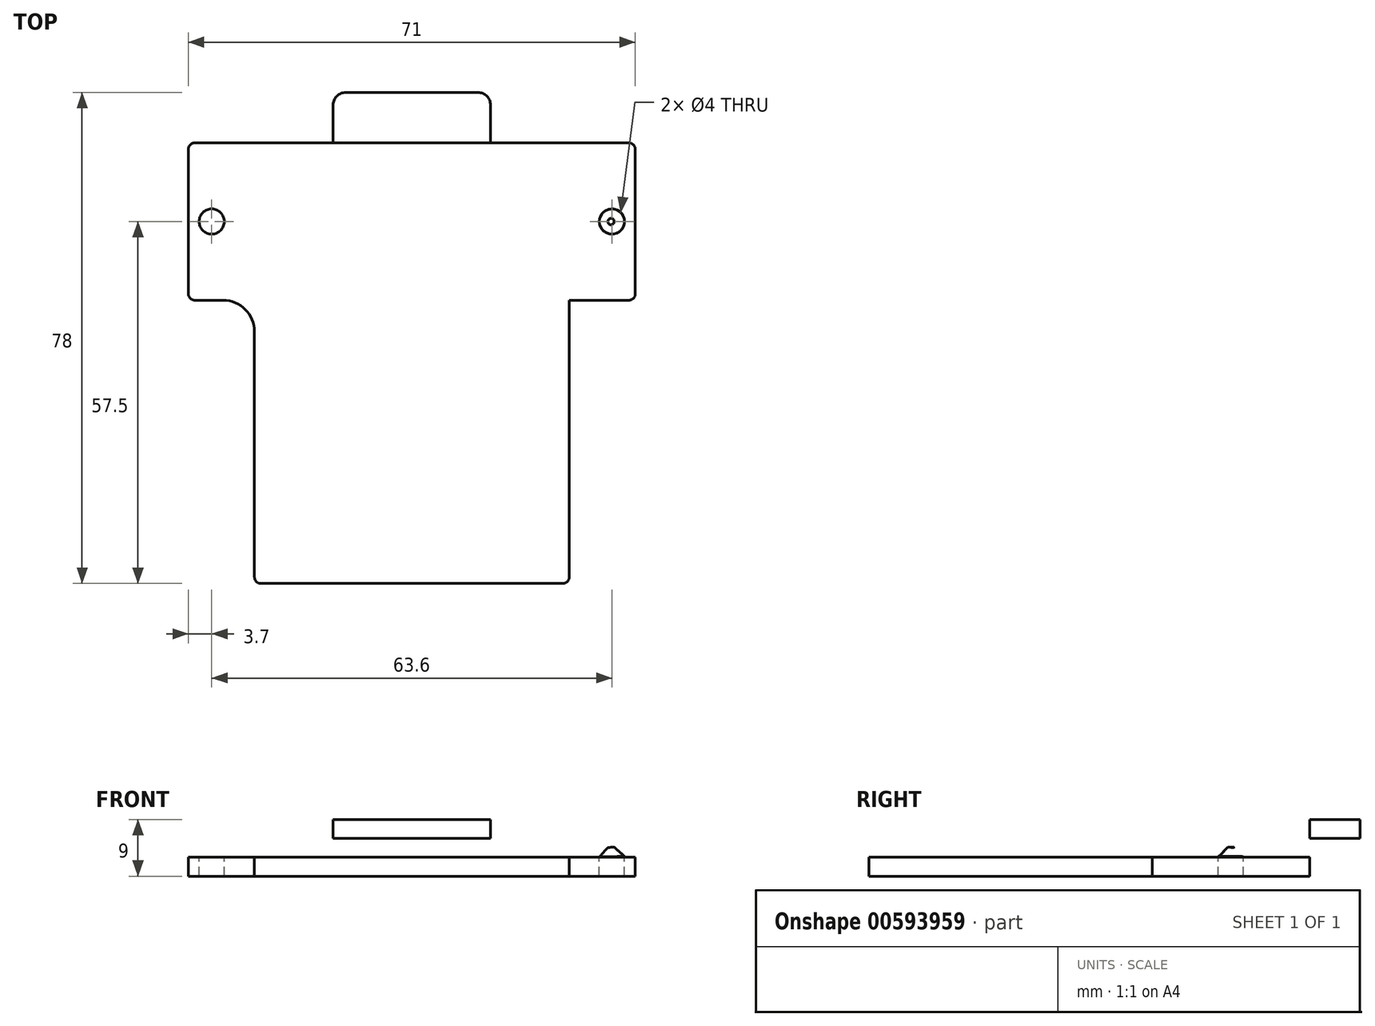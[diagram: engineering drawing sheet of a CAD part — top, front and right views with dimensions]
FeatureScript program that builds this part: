
annotation { "Feature Type Name" : "Feature", "Feature Type Description" : "" }
export const myFeature = defineFeature(function(context is Context, id is Id, definition is map)
    precondition{}
    {
        {
            var Q0;
            Q0=qCreatedBy(makeId("Top.planeOp"),FACE);
            var sketch = newSketch(context, id + "F0", { "sketchPlane" : qUnion([Q0])});
            skLineSegment(sketch, "E0.bottom", {"start": v(-35.5, 12.5) * mm, "end": v(35.5, 12.5) * mm});
            skLineSegment(sketch, "E0.top", {"start": v(-35.5, -12.5) * mm, "end": v(35.5, -12.5) * mm});
            skLineSegment(sketch, "E0.left", {"start": v(-35.5, 12.5) * mm, "end": v(-35.5, -12.5) * mm});
            skLineSegment(sketch, "E0.right", {"start": v(35.5, 12.5) * mm, "end": v(35.5, -12.5) * mm});
            skPoint(sketch, "E0.middle", {"position": v(0, 0) * mm});
            skCircle(sketch, "E1", {"center": v(-31.8, 0) * mm, "radius": 2 * mm});
            skCircle(sketch, "E2.MirrorC", {"center": v(31.8, 0) * mm, "radius": 2 * mm});
            skSolve(sketch);
        }
        {
            var Q0;
            Q0=makeQuery(id+"F0.imprint","IMPRINT",FACE,{"disambiguationData":[TD([[makeQuery(id+"F0.imprint","IMPRINT",EDGE,{"derivedFrom":sQuery(id+"F0.wireOp",EDGE,"E0.bottom")}),-1.0]])]});
            extrude(context, id + "F1", {"entities" : qUnion([Q0]), "oppositeDirection" : true, "depth" : 3 * mm, "offsetDistance" : 25 * mm});
        }
        {
            var Q0;
            Q0=qCreatedBy(makeId("Front.planeOp"),FACE);
            var sketch = newSketch(context, id + "F2", { "sketchPlane" : qUnion([Q0])});
            skLineSegment(sketch, "E3", {"start": v(-35.49, 0) * mm, "end": v(-35.49, 2) * mm});
            skLineSegment(sketch, "E4.MirrorCS", {"start": v(35.49, 0) * mm, "end": v(35.49, 2) * mm});
            skArc(sketch, "E5", {"start": v(-35.49, 2) * mm, "mid": v(0, 0) * mm, "end": v(35.49, 2) * mm});
            skLineSegment(sketch, "E6", {"start": v(-35.49, 0) * mm, "end": v(35.49, 0) * mm});
            skSolve(sketch);
        }
        {
            var Q0;
            {var subQ0=sQuery(id+"F2.wireOp",EDGE,"E3");Q0=makeQuery(id+"F2.imprint","IMPRINT",FACE,{"disambiguationData":[TD([[makeQuery(id+"F2.imprint","IMPRINT",EDGE,{"derivedFrom":subQ0}),-1.0]])]});}
            var Q1;
            {var subQ0=sQuery(id+"F2.wireOp",EDGE,"E4.MirrorCS");Q1=makeQuery(id+"F2.imprint","IMPRINT",FACE,{"disambiguationData":[TD([[makeQuery(id+"F2.imprint","IMPRINT",EDGE,{"derivedFrom":subQ0}),1.0]])]});}
            extrude(context, id + "F3", {"entities" : qUnion([Q0, Q1]), "operationType" : NewBodyOperationType.ADD, "endBound" : BoundingType.SYMMETRIC, "depth" : 25 * mm, "offsetDistance" : 25 * mm});
        }
        {
            var Q0;
            Q0=qCreatedBy(makeId("Top.planeOp"),FACE);
            var sketch = newSketch(context, id + "F4", { "sketchPlane" : qUnion([Q0])});
            skLineSegment(sketch, "E7.bottom", {"start": v(-12.5, 20.5) * mm, "end": v(12.5, 20.5) * mm});
            skLineSegment(sketch, "E7.top", {"start": v(-12.5, 4.5) * mm, "end": v(12.5, 4.5) * mm});
            skLineSegment(sketch, "E7.left", {"start": v(-12.5, 20.5) * mm, "end": v(-12.5, 4.5) * mm});
            skLineSegment(sketch, "E7.right", {"start": v(12.5, 20.5) * mm, "end": v(12.5, 4.5) * mm});
            skPoint(sketch, "E7.middle", {"position": v(0, 12.5) * mm});
            skSolve(sketch);
        }
        {
            var Q0;
            Q0=makeQuery(id+"F4.imprint","IMPRINT",FACE,{"disambiguationData":[TD([[makeQuery(id+"F4.imprint","IMPRINT",EDGE,{"derivedFrom":sQuery(id+"F4.wireOp",EDGE,"E7.bottom")}),-1.0]])]});
            extrude(context, id + "F5", {"entities" : qUnion([Q0]), "operationType" : NewBodyOperationType.ADD, "depth" : 6 * mm, "offsetDistance" : 25 * mm});
        }
        {
            var Q0;
            Q0=makeQuery(id+"F5.opExtrude","SWEPT_FACE",FACE,{"disambiguationData":[OSD([sQuery(id+"F4.wireOp",EDGE,"E7.bottom")])]});
            var sketch = newSketch(context, id + "F6", { "sketchPlane" : qUnion([Q0])});
            skLineSegment(sketch, "E8.bottom", {"start": v(12.5, 0) * mm, "end": v(-12.5, 0) * mm});
            skLineSegment(sketch, "E8.top", {"start": v(12.5, 3) * mm, "end": v(-12.5, 3) * mm});
            skLineSegment(sketch, "E8.left", {"start": v(12.5, 0) * mm, "end": v(12.5, 3) * mm});
            skLineSegment(sketch, "E8.right", {"start": v(-12.5, 0) * mm, "end": v(-12.5, 3) * mm});
            skSolve(sketch);
        }
        {
            var Q0;
            Q0=makeQuery(id+"F6.imprint","IMPRINT",FACE,{"disambiguationData":[TD([[makeQuery(id+"F6.imprint","IMPRINT",EDGE,{"derivedFrom":sQuery(id+"F6.wireOp",EDGE,"E8.bottom")}),-1.0]])]});
            extrude(context, id + "F7", {"entities" : qUnion([Q0]), "operationType" : NewBodyOperationType.REMOVE, "oppositeDirection" : true, "depth" : 8 * mm, "offsetDistance" : 25 * mm});
        }
        {
            var Q0;
            Q0=makeQuery(id+"F5.opExtrude","SWEPT_EDGE",EDGE,{"disambiguationData":[OSD([sQuery(id+"F4.wireOp",EDGE,"E7.bottom"),sQuery(id+"F4.wireOp",EDGE,"E7.right")])]});
            var Q1;
            Q1=makeQuery(id+"F5.opExtrude","SWEPT_EDGE",EDGE,{"disambiguationData":[OSD([sQuery(id+"F4.wireOp",EDGE,"E7.bottom"),sQuery(id+"F4.wireOp",EDGE,"E7.left")])]});
            fillet(context, id + "F8", {"entities" : qUnion([Q0, Q1]), "radius" : 2 * mm, "tangentPropagation" : true, "allowEdgeOverflow" : false});
        }
        {
            var Q0;
            {var subQ0=sQuery(id+"F2.wireOp",EDGE,"E5");Q0=makeQuery(id+"F5.boolean.opBoolean","INTERSECT",EDGE,{"derivedFrom":[makeQuery(id+"F3.boolean.opBoolean","MERGE",FACE,{"derivedFrom":[makeQuery(id+"F3.opExtrude","SWEPT_FACE",FACE,{"disambiguationData":[OSD([subQ0]),TDD([makeQuery(id+"F2.imprint","IMPRINT",EDGE,{"disambiguationData":[TD([[makeQuery(id+"F2.imprint","INTERSECT",VERTEX,{"derivedFrom":[sQuery(id+"F2.wireOp",EDGE,"E3"),subQ0]}),-1.0]])],"derivedFrom":subQ0})])]}),makeQuery(id+"F3.opExtrude","SWEPT_FACE",FACE,{"disambiguationData":[OSD([subQ0]),TDD([makeQuery(id+"F2.imprint","IMPRINT",EDGE,{"disambiguationData":[TD([[makeQuery(id+"F2.imprint","INTERSECT",VERTEX,{"derivedFrom":[sQuery(id+"F2.wireOp",EDGE,"E4.MirrorCS"),subQ0]}),1.0]])],"derivedFrom":subQ0})])]})]}),makeQuery(id+"F5.opExtrude","SWEPT_FACE",FACE,{"disambiguationData":[OSD([sQuery(id+"F4.wireOp",EDGE,"E7.top")])]})]});}
            chamfer(context, id + "F9", {"entities" : qUnion([Q0]), "width" : 6 * mm, "tangentPropagation" : true});
        }
        {
            var Q0;
            Q0=makeQuery(id+"F0.imprint","IMPRINT",FACE,{"disambiguationData":[TD([[makeQuery(id+"F0.imprint","IMPRINT",EDGE,{"derivedFrom":sQuery(id+"F0.wireOp",EDGE,"E2.MirrorC")}),-1.0]])]});
            var Q1;
            Q1=makeQuery(id+"F0.imprint","IMPRINT",FACE,{"disambiguationData":[TD([[makeQuery(id+"F0.imprint","IMPRINT",EDGE,{"derivedFrom":sQuery(id+"F0.wireOp",EDGE,"E1")}),1.0]])]});
            extrude(context, id + "F10", {"entities" : qUnion([Q0, Q1]), "operationType" : NewBodyOperationType.REMOVE, "depth" : 25 * mm, "offsetDistance" : 25 * mm});
        }
        {
            var Q0;
            {var subQ0=sQuery(id+"F2.wireOp",EDGE,"E5");Q0=makeQuery(id+"F10.boolean.opBoolean","INTERSECT",EDGE,{"derivedFrom":[makeQuery(id+"F3.boolean.opBoolean","MERGE",FACE,{"derivedFrom":[makeQuery(id+"F3.opExtrude","SWEPT_FACE",FACE,{"disambiguationData":[OSD([subQ0]),TDD([makeQuery(id+"F2.imprint","IMPRINT",EDGE,{"disambiguationData":[TD([[makeQuery(id+"F2.imprint","INTERSECT",VERTEX,{"derivedFrom":[sQuery(id+"F2.wireOp",EDGE,"E3"),subQ0]}),-1.0]])],"derivedFrom":subQ0})])]}),makeQuery(id+"F3.opExtrude","SWEPT_FACE",FACE,{"disambiguationData":[OSD([subQ0]),TDD([makeQuery(id+"F2.imprint","IMPRINT",EDGE,{"disambiguationData":[TD([[makeQuery(id+"F2.imprint","INTERSECT",VERTEX,{"derivedFrom":[sQuery(id+"F2.wireOp",EDGE,"E4.MirrorCS"),subQ0]}),1.0]])],"derivedFrom":subQ0})])]})]}),makeQuery(id+"F10.opExtrude","SWEPT_FACE",FACE,{"disambiguationData":[OSD([sQuery(id+"F0.wireOp",EDGE,"E1")])]})]});}
            var Q1;
            {var subQ0=sQuery(id+"F2.wireOp",EDGE,"E5");Q1=makeQuery(id+"F10.boolean.opBoolean","INTERSECT",EDGE,{"derivedFrom":[makeQuery(id+"F3.boolean.opBoolean","MERGE",FACE,{"derivedFrom":[makeQuery(id+"F3.opExtrude","SWEPT_FACE",FACE,{"disambiguationData":[OSD([subQ0]),TDD([makeQuery(id+"F2.imprint","IMPRINT",EDGE,{"disambiguationData":[TD([[makeQuery(id+"F2.imprint","INTERSECT",VERTEX,{"derivedFrom":[sQuery(id+"F2.wireOp",EDGE,"E3"),subQ0]}),-1.0]])],"derivedFrom":subQ0})])]}),makeQuery(id+"F3.opExtrude","SWEPT_FACE",FACE,{"disambiguationData":[OSD([subQ0]),TDD([makeQuery(id+"F2.imprint","IMPRINT",EDGE,{"disambiguationData":[TD([[makeQuery(id+"F2.imprint","INTERSECT",VERTEX,{"derivedFrom":[sQuery(id+"F2.wireOp",EDGE,"E4.MirrorCS"),subQ0]}),1.0]])],"derivedFrom":subQ0})])]})]}),makeQuery(id+"F10.opExtrude","SWEPT_FACE",FACE,{"disambiguationData":[OSD([sQuery(id+"F0.wireOp",EDGE,"E2.MirrorC")])]})]});}
            chamfer(context, id + "F11", {"entities" : qUnion([Q0, Q1]), "width" : 1.5 * mm, "tangentPropagation" : true});
        }
        {
            var Q0;
            {var subQ0=sQuery(id+"F2.wireOp",EDGE,"E6");var subQ1=sQuery(id+"F2.wireOp",EDGE,"E5");Q0=makeQuery(id+"F3.boolean.opBoolean","MERGE",FACE,{"derivedFrom":[makeQuery(id+"F1.opExtrude","SWEPT_FACE",FACE,{"disambiguationData":[OSD([sQuery(id+"F0.wireOp",EDGE,"E0.top")])]}),makeQuery(id+"F3.opExtrude","CAP_FACE",FACE,{"disambiguationData":[OSD([sQuery(id+"F2.wireOp",EDGE,"E3"),subQ1,subQ0])],"isStart":false}),makeQuery(id+"F3.opExtrude","CAP_FACE",FACE,{"disambiguationData":[OSD([sQuery(id+"F2.wireOp",EDGE,"E4.MirrorCS"),subQ1,subQ0])],"isStart":false})]});}
            var sketch = newSketch(context, id + "F12", { "sketchPlane" : qUnion([Q0])});
            skLineSegment(sketch, "E9", {"start": v(25, -3) * mm, "end": v(25, 1) * mm});
            skLineSegment(sketch, "E10.MirrorCS", {"start": v(-25, -3) * mm, "end": v(-25, 1) * mm});
            skSolve(sketch);
        }
        {
            var Q0;
            {var subQ0=sQuery(id+"F12.wireOp",EDGE,"E9");Q0=makeQuery(id+"F12.imprint","IMPRINT",FACE,{"disambiguationData":[TD([[makeQuery(id+"F12.imprint","IMPRINT",EDGE,{"derivedFrom":subQ0}),1.0]])]});}
            extrude(context, id + "F13", {"entities" : qUnion([Q0]), "operationType" : NewBodyOperationType.ADD, "depth" : 45 * mm, "offsetDistance" : 25 * mm});
        }
        {
            var Q0;
            Q0=makeQuery(id+"F13.opExtrude","CAP_EDGE",EDGE,{"disambiguationData":[OSD([sQuery(id+"F12.wireOp",EDGE,"E10.MirrorCS")])],"isStart":true});
            var Q1;
            Q1=makeQuery(id+"F13.opExtrude","CAP_EDGE",EDGE,{"disambiguationData":[OSD([sQuery(id+"F12.wireOp",EDGE,"E9")])],"isStart":true});
            fillet(context, id + "F14", {"entities" : qUnion([Q0, Q1]), "radius" : 5 * mm, "tangentPropagation" : true, "allowEdgeOverflow" : false});
        }
        {
            var Q0;
            Q0=makeQuery(id+"F1.opExtrude","SWEPT_EDGE",EDGE,{"disambiguationData":[OSD([sQuery(id+"F0.wireOp",EDGE,"E0.bottom"),sQuery(id+"F0.wireOp",EDGE,"E0.left")])]});
            var Q1;
            Q1=makeQuery(id+"F1.opExtrude","SWEPT_EDGE",EDGE,{"disambiguationData":[OSD([sQuery(id+"F0.wireOp",EDGE,"E0.top"),sQuery(id+"F0.wireOp",EDGE,"E0.left")])]});
            var Q2;
            Q2=makeQuery(id+"F1.opExtrude","SWEPT_EDGE",EDGE,{"disambiguationData":[OSD([sQuery(id+"F0.wireOp",EDGE,"E0.bottom"),sQuery(id+"F0.wireOp",EDGE,"E0.right")])]});
            var Q3;
            Q3=makeQuery(id+"F1.opExtrude","SWEPT_EDGE",EDGE,{"disambiguationData":[OSD([sQuery(id+"F0.wireOp",EDGE,"E0.top"),sQuery(id+"F0.wireOp",EDGE,"E0.right")])]});
            var Q4;
            Q4=makeQuery(id+"F13.opExtrude","CAP_EDGE",EDGE,{"disambiguationData":[OSD([sQuery(id+"F12.wireOp",EDGE,"E9")])],"isStart":false});
            var Q5;
            Q5=makeQuery(id+"F13.opExtrude","CAP_EDGE",EDGE,{"disambiguationData":[OSD([sQuery(id+"F12.wireOp",EDGE,"E10.MirrorCS")])],"isStart":false});
            fillet(context, id + "F15", {"entities" : qUnion([Q0, Q1, Q2, Q3, Q4, Q5]), "radius" : 1 * mm, "tangentPropagation" : true, "allowEdgeOverflow" : false});
        }
    });
